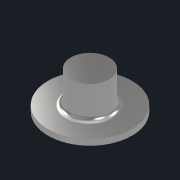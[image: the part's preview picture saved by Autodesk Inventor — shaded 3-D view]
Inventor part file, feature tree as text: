
AUTODESK INVENTOR PART (.ipt)
format: ipt  version: 2022.2 (Build 262287010, 287A)  size: 103,424 bytes
history: native  units: mm
features: extrude x2, sketch x2, fillet x1
ambient origin geometry x8: Origin, YZ Plane, XZ Plane, XY Plane, X Axis, Y Axis, Z Axis, Center Point
bodies: Solid1 (feature_tree)
feature tree (5):
  extrude  "Extrusion1"  Depth=1.2mm TaperAngle=0.0deg
  extrude  "Extrusion2"  Depth=6.6mm TaperAngle=0.0deg
  fillet  "Fillet1"  Radius=1.0mm
  sketch  "Sketch1"  dims[d0=17.5mm d1=1.2mm d2=0.0mm]
  sketch  "Sketch2"  dims[d3=8.0mm d4=6.6mm d5=0.0mm d6=1.0mm]
